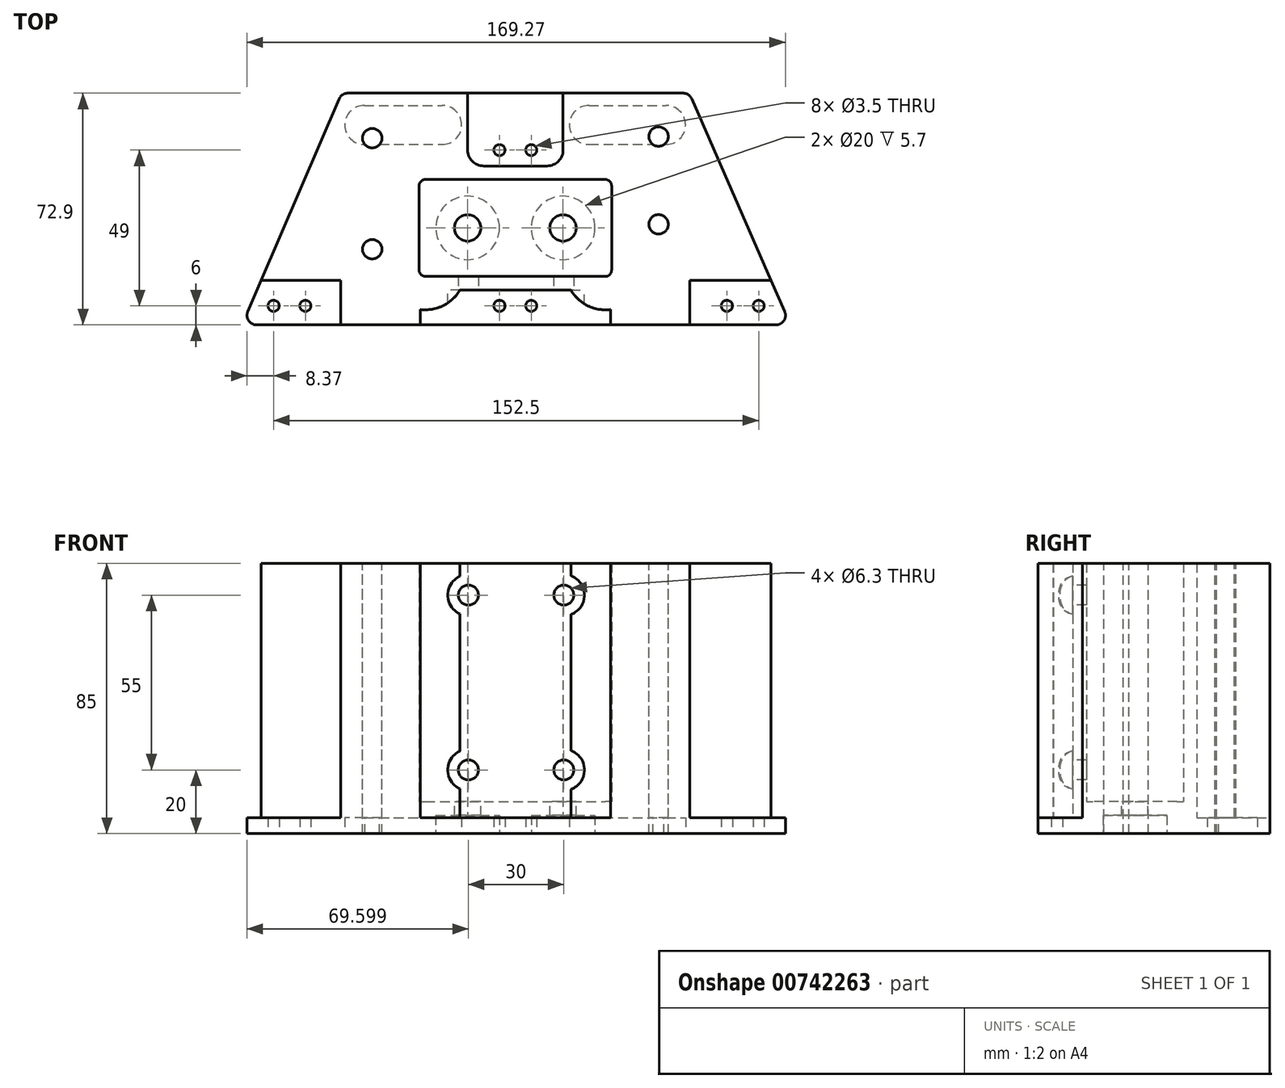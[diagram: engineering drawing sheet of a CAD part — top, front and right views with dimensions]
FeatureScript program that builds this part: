
annotation { "Feature Type Name" : "Feature", "Feature Type Description" : "" }
export const myFeature = defineFeature(function(context is Context, id is Id, definition is map)
    precondition{}
    {
        {
            var Q0;
            Q0=qCreatedBy(makeId("Top.planeOp"),FACE);
            var sketch = newSketch(context, id + "F0", { "sketchPlane" : qUnion([Q0])});
            skCircle(sketch, "E0", {"center": v(-5, 0) * mm, "radius": 1.75 * mm});
            skCircle(sketch, "E1", {"center": v(5, 0) * mm, "radius": 1.75 * mm});
            skLineSegment(sketch, "E2", {"start": v(-5, 0) * mm, "end": v(5, 0) * mm, "construction": true});
            skLineSegment(sketch, "E3.bottom", {"start": v(-47.48, 14.05) * mm, "end": v(-23.02, 14.05) * mm});
            skLineSegment(sketch, "E3.top", {"start": v(-47.48, 1.75) * mm, "end": v(-23.02, 1.75) * mm});
            skLineSegment(sketch, "E3.left", {"start": v(-47.48, 14.05) * mm, "end": v(-47.48, 1.75) * mm, "construction": true});
            skLineSegment(sketch, "E3.right", {"start": v(-23.02, 14.05) * mm, "end": v(-23.02, 1.75) * mm, "construction": true});
            skLineSegment(sketch, "E4", {"start": v(-5, 1.75) * mm, "end": v(-23.02, 1.75) * mm, "construction": true});
            skArc(sketch, "E5", {"start": v(-47.48, 14.05) * mm, "mid": v(-53.63, 7.9) * mm, "end": v(-47.48, 1.75) * mm});
            skArc(sketch, "E6", {"start": v(-23.02, 14.05) * mm, "mid": v(-16.88, 7.9) * mm, "end": v(-23.02, 1.75) * mm});
            skLineSegment(sketch, "E7", {"start": v(-53.63, 7.9) * mm, "end": v(-16.88, 7.9) * mm, "construction": true});
            skLineSegment(sketch, "E8", {"start": v(-16.88, 7.9) * mm, "end": v(-16.88, 1.75) * mm, "construction": true});
            skLineSegment(sketch, "E9", {"start": v(-5, 0) * mm, "end": v(-5, 1.75) * mm, "construction": true});
            skLineSegment(sketch, "E10.bottom", {"start": v(23.15, 14.05) * mm, "end": v(47.35, 14.05) * mm});
            skLineSegment(sketch, "E10.top", {"start": v(23.15, 1.75) * mm, "end": v(47.35, 1.75) * mm});
            skLineSegment(sketch, "E10.left", {"start": v(23.15, 14.05) * mm, "end": v(23.15, 1.75) * mm, "construction": true});
            skLineSegment(sketch, "E10.right", {"start": v(47.35, 14.05) * mm, "end": v(47.35, 1.75) * mm, "construction": true});
            skArc(sketch, "E11", {"start": v(23.15, 14.05) * mm, "mid": v(17, 7.9) * mm, "end": v(23.15, 1.75) * mm});
            skArc(sketch, "E12", {"start": v(47.35, 14.05) * mm, "mid": v(53.5, 7.9) * mm, "end": v(47.35, 1.75) * mm});
            skLineSegment(sketch, "E13", {"start": v(17, 7.9) * mm, "end": v(53.5, 7.9) * mm, "construction": true});
            skLineSegment(sketch, "E14", {"start": v(23.15, 1.75) * mm, "end": v(5, 1.75) * mm, "construction": true});
            skLineSegment(sketch, "E15", {"start": v(5, 0) * mm, "end": v(5, 1.75) * mm, "construction": true});
            skLineSegment(sketch, "E16", {"start": v(17, 7.9) * mm, "end": v(17, 1.75) * mm, "construction": true});
            skLineSegment(sketch, "E17", {"start": v(-5, 0) * mm, "end": v(-5, -49) * mm, "construction": true});
            skCircle(sketch, "E18", {"center": v(-5, -49) * mm, "radius": 1.75 * mm});
            skLineSegment(sketch, "E19", {"start": v(-5, -49) * mm, "end": v(5, -49) * mm, "construction": true});
            skCircle(sketch, "E20", {"center": v(5, -49) * mm, "radius": 1.75 * mm});
            skLineSegment(sketch, "E21", {"start": v(-5, -49) * mm, "end": v(-66, -49) * mm, "construction": true});
            skLineSegment(sketch, "E22", {"start": v(-76, -49) * mm, "end": v(-66, -49) * mm, "construction": true});
            skLineSegment(sketch, "E23", {"start": v(5, -49) * mm, "end": v(66.5, -49) * mm, "construction": true});
            skLineSegment(sketch, "E24", {"start": v(66.5, -49) * mm, "end": v(76.5, -49) * mm, "construction": true});
            skCircle(sketch, "E25", {"center": v(76.5, -49) * mm, "radius": 1.75 * mm});
            skCircle(sketch, "E26", {"center": v(66.5, -49) * mm, "radius": 1.75 * mm});
            skCircle(sketch, "E27", {"center": v(-76, -49) * mm, "radius": 1.75 * mm});
            skCircle(sketch, "E28", {"center": v(-66, -49) * mm, "radius": 1.75 * mm});
            skLineSegment(sketch, "E29", {"start": v(-55.42, 16.08) * mm, "end": v(-84.12, -50.82) * mm});
            skLineSegment(sketch, "E30", {"start": v(-81.37, -55) * mm, "end": v(81.9, -55) * mm});
            skLineSegment(sketch, "E31", {"start": v(84.65, -50.8) * mm, "end": v(55.43, 16.1) * mm});
            skLineSegment(sketch, "E32", {"start": v(52.68, 17.9) * mm, "end": v(-52.67, 17.9) * mm});
            skLineSegment(sketch, "E33", {"start": v(0, 0) * mm, "end": v(0, 17.9) * mm, "construction": true});
            skPoint(sketch, "E34.visualSharp", {"position": v(-85.92, -55) * mm});
            skArc(sketch, "E34.filletArc", {"start": v(-84.12, -50.82) * mm, "mid": v(-83.87, -53.65) * mm, "end": v(-81.37, -55) * mm});
            skPoint(sketch, "E35.visualSharp", {"position": v(-54.64, 17.9) * mm});
            skArc(sketch, "E35.filletArc", {"start": v(-52.67, 17.9) * mm, "mid": v(-54.32, 17.4) * mm, "end": v(-55.42, 16.08) * mm});
            skPoint(sketch, "E36.visualSharp", {"position": v(54.64, 17.9) * mm});
            skArc(sketch, "E36.filletArc", {"start": v(55.43, 16.1) * mm, "mid": v(54.32, 17.41) * mm, "end": v(52.68, 17.9) * mm});
            skPoint(sketch, "E37.visualSharp", {"position": v(86.49, -55) * mm});
            skArc(sketch, "E37.filletArc", {"start": v(81.9, -55) * mm, "mid": v(84.41, -53.64) * mm, "end": v(84.65, -50.8) * mm});
            skLineSegment(sketch, "E38", {"start": v(-77.6, -48.31) * mm, "end": v(-82.2, -46.34) * mm, "construction": true});
            skLineSegment(sketch, "E39", {"start": v(-77.6, -48.31) * mm, "end": v(-76, -49) * mm, "construction": true});
            skLineSegment(sketch, "E40", {"start": v(76.5, -49) * mm, "end": v(78.1, -48.3) * mm, "construction": true});
            skLineSegment(sketch, "E41", {"start": v(78.1, -48.3) * mm, "end": v(82.69, -46.3) * mm, "construction": true});
            skLineSegment(sketch, "E42", {"start": v(0, 0) * mm, "end": v(0, -49) * mm, "construction": true});
            skPoint(sketch, "E43", {"position": v(-35.25, 7.9) * mm});
            skPoint(sketch, "E44", {"position": v(35.25, 7.9) * mm});
            skSolve(sketch);
        }
        {
            var Q0;
            Q0 = qSketchRegion(id + "F0", true);
            var Q1;
            Q1=makeQuery(id+"F0.imprint","IMPRINT",FACE,{"disambiguationData":[TD([[makeQuery(id+"F0.imprint","IMPRINT",EDGE,{"derivedFrom":sQuery(id+"F0.wireOp",EDGE,"E3.bottom")}),-1.0]])]});
            var Q2;
            Q2=makeQuery(id+"F0.imprint","IMPRINT",FACE,{"disambiguationData":[TD([[makeQuery(id+"F0.imprint","IMPRINT",EDGE,{"derivedFrom":sQuery(id+"F0.wireOp",EDGE,"E10.bottom")}),-1.0]])]});
            extrude(context, id + "F1", {"entities" : qUnion([Q0, Q1, Q2]), "depth" : 5 * mm, "offsetDistance" : 25 * mm});
        }
        {
            var Q0;
            Q0=makeQuery(id+"F1.opExtrude","CAP_FACE",FACE,{"disambiguationData":[OSD([sQuery(id+"F0.wireOp",EDGE,"E0"),sQuery(id+"F0.wireOp",EDGE,"E1"),sQuery(id+"F0.wireOp",EDGE,"E18"),sQuery(id+"F0.wireOp",EDGE,"E20"),sQuery(id+"F0.wireOp",EDGE,"E25"),sQuery(id+"F0.wireOp",EDGE,"E26"),sQuery(id+"F0.wireOp",EDGE,"E27"),sQuery(id+"F0.wireOp",EDGE,"E28"),sQuery(id+"F0.wireOp",EDGE,"E29"),sQuery(id+"F0.wireOp",EDGE,"E30"),sQuery(id+"F0.wireOp",EDGE,"E31"),sQuery(id+"F0.wireOp",EDGE,"E32"),sQuery(id+"F0.wireOp",EDGE,"E34.filletArc"),sQuery(id+"F0.wireOp",EDGE,"E35.filletArc"),sQuery(id+"F0.wireOp",EDGE,"E36.filletArc"),sQuery(id+"F0.wireOp",EDGE,"E37.filletArc")])],"isStart":false});
            var sketch = newSketch(context, id + "F2", { "sketchPlane" : qUnion([Q0])});
            skLineSegment(sketch, "E45.bottom", {"start": v(-28.25, -9.25) * mm, "end": v(28.25, -9.25) * mm});
            skLineSegment(sketch, "E45.top", {"start": v(-28.25, -39.75) * mm, "end": v(28.25, -39.75) * mm});
            skLineSegment(sketch, "E45.left", {"start": v(-30.25, -11.25) * mm, "end": v(-30.25, -37.75) * mm});
            skLineSegment(sketch, "E45.right", {"start": v(30.25, -11.25) * mm, "end": v(30.25, -37.75) * mm});
            skPoint(sketch, "E46.visualSharp", {"position": v(-30.25, -9.25) * mm});
            skArc(sketch, "E46.filletArc", {"start": v(-28.25, -9.25) * mm, "mid": v(-29.66, -9.84) * mm, "end": v(-30.25, -11.25) * mm});
            skPoint(sketch, "E47.visualSharp", {"position": v(30.25, -9.25) * mm});
            skArc(sketch, "E47.filletArc", {"start": v(30.25, -11.25) * mm, "mid": v(29.66, -9.84) * mm, "end": v(28.25, -9.25) * mm});
            skPoint(sketch, "E48.visualSharp", {"position": v(30.25, -39.75) * mm});
            skArc(sketch, "E48.filletArc", {"start": v(28.25, -39.75) * mm, "mid": v(29.66, -39.16) * mm, "end": v(30.25, -37.75) * mm});
            skPoint(sketch, "E49.visualSharp", {"position": v(-30.25, -39.75) * mm});
            skArc(sketch, "E49.filletArc", {"start": v(-30.25, -37.75) * mm, "mid": v(-29.66, -39.16) * mm, "end": v(-28.25, -39.75) * mm});
            skLineSegment(sketch, "E50.0", {"start": v(-28.05, -11.45) * mm, "end": v(28.05, -11.45) * mm, "construction": true});
            skLineSegment(sketch, "E50.1", {"start": v(-28.05, -11.45) * mm, "end": v(-28.05, -37.55) * mm, "construction": true});
            skLineSegment(sketch, "E50.2", {"start": v(-28.05, -37.55) * mm, "end": v(28.05, -37.55) * mm, "construction": true});
            skLineSegment(sketch, "E50.3", {"start": v(28.05, -11.45) * mm, "end": v(28.05, -37.55) * mm, "construction": true});
            skLineSegment(sketch, "E51", {"start": v(-30.25, -24.5) * mm, "end": v(30.25, -24.5) * mm, "construction": true});
            skCircle(sketch, "E52", {"center": v(-15, -24.5) * mm, "radius": 4.15 * mm});
            skCircle(sketch, "E53", {"center": v(15, -24.5) * mm, "radius": 4.15 * mm});
            skLineSegment(sketch, "E54.0", {"start": v(-55.42, 16.08) * mm, "end": v(-84.12, -50.82) * mm});
            skArc(sketch, "E54.1", {"start": v(-52.67, 17.9) * mm, "mid": v(-54.32, 17.4) * mm, "end": v(-55.42, 16.08) * mm});
            skLineSegment(sketch, "E54.2", {"start": v(52.68, 17.9) * mm, "end": v(-52.67, 17.9) * mm});
            skArc(sketch, "E54.3", {"start": v(55.43, 16.1) * mm, "mid": v(54.32, 17.41) * mm, "end": v(52.68, 17.9) * mm});
            skLineSegment(sketch, "E54.4", {"start": v(84.65, -50.8) * mm, "end": v(55.43, 16.1) * mm});
            skArc(sketch, "E54.5", {"start": v(81.9, -55) * mm, "mid": v(84.41, -53.64) * mm, "end": v(84.65, -50.8) * mm});
            skLineSegment(sketch, "E54.6", {"start": v(-81.37, -55) * mm, "end": v(81.9, -55) * mm});
            skArc(sketch, "E54.7", {"start": v(-84.12, -50.82) * mm, "mid": v(-83.87, -53.65) * mm, "end": v(-81.37, -55) * mm});
            skArc(sketch, "E55", {"start": v(17.42, -44) * mm, "mid": v(29.87, -50.14) * mm, "end": v(40.32, -41) * mm});
            skArc(sketch, "E56", {"start": v(-40.32, -41) * mm, "mid": v(-29.87, -50.14) * mm, "end": v(-17.42, -44) * mm});
            skLineSegment(sketch, "E57", {"start": v(-79.91, -41) * mm, "end": v(-40.32, -41) * mm});
            skLineSegment(sketch, "E58", {"start": v(-17.42, -44) * mm, "end": v(17.42, -44) * mm});
            skLineSegment(sketch, "E59", {"start": v(-15, -5) * mm, "end": v(15, -5) * mm});
            skLineSegment(sketch, "E60", {"start": v(-15, -5) * mm, "end": v(-15, 17.9) * mm});
            skLineSegment(sketch, "E61", {"start": v(15, -5) * mm, "end": v(15, 17.9) * mm});
            skLineSegment(sketch, "E62", {"start": v(40.32, -41) * mm, "end": v(80.37, -41) * mm});
            skPoint(sketch, "E63", {"position": v(0, -5) * mm});
            skSolve(sketch);
        }
        {
            var Q0;
            Q0=makeQuery(id+"F2.imprint","IMPRINT",FACE,{"disambiguationData":[TD([[makeQuery(id+"F2.imprint","IMPRINT",EDGE,{"derivedFrom":sQuery(id+"F2.wireOp",EDGE,"E45.bottom")}),1.0]])]});
            extrude(context, id + "F3", {"entities" : qUnion([Q0]), "operationType" : NewBodyOperationType.ADD, "depth" : 80 * mm, "offsetDistance" : 25 * mm});
        }
        {
            var Q0;
            Q0=makeQuery(id+"F2.imprint","IMPRINT",FACE,{"disambiguationData":[TD([[makeQuery(id+"F2.imprint","IMPRINT",EDGE,{"derivedFrom":sQuery(id+"F2.wireOp",EDGE,"E52")}),1.0]])]});
            var Q1;
            Q1=makeQuery(id+"F2.imprint","IMPRINT",FACE,{"disambiguationData":[TD([[makeQuery(id+"F2.imprint","IMPRINT",EDGE,{"derivedFrom":sQuery(id+"F2.wireOp",EDGE,"E53")}),1.0]])]});
            extrude(context, id + "F4", {"entities" : qUnion([Q0, Q1]), "operationType" : NewBodyOperationType.REMOVE, "endBound" : BoundingType.THROUGH_ALL, "oppositeDirection" : true, "depth" : 25 * mm, "offsetDistance" : 25 * mm});
        }
        {
            var Q0;
            Q0=makeQuery(id+"F3.opExtrude","SWEPT_FACE",FACE,{"disambiguationData":[OSD([sQuery(id+"F2.wireOp",EDGE,"E58")])]});
            var sketch = newSketch(context, id + "F5", { "sketchPlane" : qUnion([Q0])});
            skLineSegment(sketch, "E64", {"start": v(-79.91, 20) * mm, "end": v(80.37, 20) * mm, "construction": true});
            skLineSegment(sketch, "E65", {"start": v(-79.91, 75) * mm, "end": v(80.37, 75) * mm, "construction": true});
            skCircle(sketch, "E66", {"center": v(-14.77, 75) * mm, "radius": 3.15 * mm});
            skCircle(sketch, "E67", {"center": v(15.23, 75) * mm, "radius": 3.15 * mm});
            skCircle(sketch, "E68", {"center": v(-14.77, 20) * mm, "radius": 3.15 * mm});
            skCircle(sketch, "E69", {"center": v(15.23, 20) * mm, "radius": 3.15 * mm});
            skLineSegment(sketch, "E70", {"start": v(-14.77, 75) * mm, "end": v(-14.77, 20) * mm, "construction": true});
            skLineSegment(sketch, "E71", {"start": v(15.23, 75) * mm, "end": v(15.23, 20) * mm, "construction": true});
            skPoint(sketch, "E72", {"position": v(0.23, 75) * mm});
            skCircle(sketch, "E73", {"center": v(-14.77, 75) * mm, "radius": 6.5 * mm});
            skCircle(sketch, "E74", {"center": v(15.23, 75) * mm, "radius": 6.5 * mm});
            skCircle(sketch, "E75", {"center": v(15.23, 20) * mm, "radius": 6.5 * mm});
            skCircle(sketch, "E76", {"center": v(-14.77, 20) * mm, "radius": 6.5 * mm});
            skSolve(sketch);
        }
        {
            var Q0;
            {var subQ0=sQuery(id+"F5.wireOp",EDGE,"E66");var subQ1=makeQuery(id+"F3.opExtrude","SWEPT_EDGE",EDGE,{"disambiguationData":[OSD([sQuery(id+"F2.wireOp",EDGE,"E56"),sQuery(id+"F2.wireOp",EDGE,"E58")])]});var subQ2=makeQuery(id+"F5.imprint","INTERSECT",VERTEX,{"disambiguationData":[OD(0.0)],"derivedFrom":[subQ1,subQ0]});Q0=makeQuery(id+"F5.imprint","IMPRINT",FACE,{"disambiguationData":[TD([[makeQuery(id+"F5.imprint","IMPRINT",EDGE,{"disambiguationData":[TD([[subQ2,1.0]])],"derivedFrom":subQ0}),1.0]])]});}
            var Q1;
            {var subQ0=sQuery(id+"F5.wireOp",EDGE,"E67");var subQ1=makeQuery(id+"F3.opExtrude","SWEPT_EDGE",EDGE,{"disambiguationData":[OSD([sQuery(id+"F2.wireOp",EDGE,"E55"),sQuery(id+"F2.wireOp",EDGE,"E58")])]});var subQ2=makeQuery(id+"F5.imprint","INTERSECT",VERTEX,{"disambiguationData":[OD(0.0)],"derivedFrom":[subQ1,subQ0]});Q1=makeQuery(id+"F5.imprint","IMPRINT",FACE,{"disambiguationData":[TD([[makeQuery(id+"F5.imprint","IMPRINT",EDGE,{"disambiguationData":[TD([[subQ2,-1.0]])],"derivedFrom":subQ0}),1.0]])]});}
            var Q2;
            {var subQ0=sQuery(id+"F5.wireOp",EDGE,"E69");var subQ1=makeQuery(id+"F3.opExtrude","SWEPT_EDGE",EDGE,{"disambiguationData":[OSD([sQuery(id+"F2.wireOp",EDGE,"E55"),sQuery(id+"F2.wireOp",EDGE,"E58")])]});var subQ2=makeQuery(id+"F5.imprint","INTERSECT",VERTEX,{"disambiguationData":[OD(0.0)],"derivedFrom":[subQ1,subQ0]});Q2=makeQuery(id+"F5.imprint","IMPRINT",FACE,{"disambiguationData":[TD([[makeQuery(id+"F5.imprint","IMPRINT",EDGE,{"disambiguationData":[TD([[subQ2,1.0]])],"derivedFrom":subQ0}),1.0]])]});}
            var Q3;
            {var subQ0=sQuery(id+"F5.wireOp",EDGE,"E68");var subQ1=makeQuery(id+"F3.opExtrude","SWEPT_EDGE",EDGE,{"disambiguationData":[OSD([sQuery(id+"F2.wireOp",EDGE,"E56"),sQuery(id+"F2.wireOp",EDGE,"E58")])]});var subQ2=makeQuery(id+"F5.imprint","INTERSECT",VERTEX,{"disambiguationData":[OD(0.0)],"derivedFrom":[subQ1,subQ0]});Q3=makeQuery(id+"F5.imprint","IMPRINT",FACE,{"disambiguationData":[TD([[makeQuery(id+"F5.imprint","IMPRINT",EDGE,{"disambiguationData":[TD([[subQ2,-1.0]])],"derivedFrom":subQ0}),1.0]])]});}
            var Q4;
            {var subQ0=sQuery(id+"F5.wireOp",EDGE,"E68");var subQ1=makeQuery(id+"F3.opExtrude","SWEPT_EDGE",EDGE,{"disambiguationData":[OSD([sQuery(id+"F2.wireOp",EDGE,"E56"),sQuery(id+"F2.wireOp",EDGE,"E58")])]});var subQ2=makeQuery(id+"F5.imprint","INTERSECT",VERTEX,{"disambiguationData":[OD(0.0)],"derivedFrom":[subQ1,subQ0]});Q4=makeQuery(id+"F5.imprint","IMPRINT",FACE,{"disambiguationData":[TD([[makeQuery(id+"F5.imprint","IMPRINT",EDGE,{"disambiguationData":[TD([[subQ2,1.0]])],"derivedFrom":subQ0}),1.0]])]});}
            var Q5;
            {var subQ0=sQuery(id+"F5.wireOp",EDGE,"E66");var subQ1=makeQuery(id+"F3.opExtrude","SWEPT_EDGE",EDGE,{"disambiguationData":[OSD([sQuery(id+"F2.wireOp",EDGE,"E56"),sQuery(id+"F2.wireOp",EDGE,"E58")])]});var subQ2=makeQuery(id+"F5.imprint","INTERSECT",VERTEX,{"disambiguationData":[OD(0.0)],"derivedFrom":[subQ1,subQ0]});Q5=makeQuery(id+"F5.imprint","IMPRINT",FACE,{"disambiguationData":[TD([[makeQuery(id+"F5.imprint","IMPRINT",EDGE,{"disambiguationData":[TD([[subQ2,-1.0]])],"derivedFrom":subQ0}),1.0]])]});}
            var Q6;
            {var subQ0=sQuery(id+"F5.wireOp",EDGE,"E67");var subQ1=makeQuery(id+"F3.opExtrude","SWEPT_EDGE",EDGE,{"disambiguationData":[OSD([sQuery(id+"F2.wireOp",EDGE,"E55"),sQuery(id+"F2.wireOp",EDGE,"E58")])]});var subQ2=makeQuery(id+"F5.imprint","INTERSECT",VERTEX,{"disambiguationData":[OD(0.0)],"derivedFrom":[subQ1,subQ0]});Q6=makeQuery(id+"F5.imprint","IMPRINT",FACE,{"disambiguationData":[TD([[makeQuery(id+"F5.imprint","IMPRINT",EDGE,{"disambiguationData":[TD([[subQ2,1.0]])],"derivedFrom":subQ0}),1.0]])]});}
            var Q7;
            {var subQ0=sQuery(id+"F5.wireOp",EDGE,"E69");var subQ1=makeQuery(id+"F3.opExtrude","SWEPT_EDGE",EDGE,{"disambiguationData":[OSD([sQuery(id+"F2.wireOp",EDGE,"E55"),sQuery(id+"F2.wireOp",EDGE,"E58")])]});var subQ2=makeQuery(id+"F5.imprint","INTERSECT",VERTEX,{"disambiguationData":[OD(0.0)],"derivedFrom":[subQ1,subQ0]});Q7=makeQuery(id+"F5.imprint","IMPRINT",FACE,{"disambiguationData":[TD([[makeQuery(id+"F5.imprint","IMPRINT",EDGE,{"disambiguationData":[TD([[subQ2,-1.0]])],"derivedFrom":subQ0}),1.0]])]});}
            extrude(context, id + "F6", {"entities" : qUnion([Q0, Q1, Q2, Q3, Q4, Q5, Q6, Q7]), "operationType" : NewBodyOperationType.REMOVE, "oppositeDirection" : true, "depth" : 25 * mm, "offsetDistance" : 25 * mm});
        }
        {
            var Q0;
            {var subQ0=sQuery(id+"F5.wireOp",EDGE,"E67");var subQ1=makeQuery(id+"F3.opExtrude","SWEPT_EDGE",EDGE,{"disambiguationData":[OSD([sQuery(id+"F2.wireOp",EDGE,"E55"),sQuery(id+"F2.wireOp",EDGE,"E58")])]});var subQ2=makeQuery(id+"F5.imprint","INTERSECT",VERTEX,{"disambiguationData":[OD(0.0)],"derivedFrom":[subQ1,subQ0]});Q0=makeQuery(id+"F5.imprint","IMPRINT",FACE,{"disambiguationData":[TD([[makeQuery(id+"F5.imprint","IMPRINT",EDGE,{"disambiguationData":[TD([[subQ2,1.0]])],"derivedFrom":subQ0}),1.0]])]});}
            var Q1;
            {var subQ0=sQuery(id+"F5.wireOp",EDGE,"E67");var subQ1=makeQuery(id+"F3.opExtrude","SWEPT_EDGE",EDGE,{"disambiguationData":[OSD([sQuery(id+"F2.wireOp",EDGE,"E55"),sQuery(id+"F2.wireOp",EDGE,"E58")])]});var subQ2=makeQuery(id+"F5.imprint","INTERSECT",VERTEX,{"disambiguationData":[OD(0.0)],"derivedFrom":[subQ1,subQ0]});Q1=makeQuery(id+"F5.imprint","IMPRINT",FACE,{"disambiguationData":[TD([[makeQuery(id+"F5.imprint","IMPRINT",EDGE,{"disambiguationData":[TD([[subQ2,1.0]])],"derivedFrom":subQ0}),-1.0]])]});}
            var Q2;
            {var subQ0=sQuery(id+"F5.wireOp",EDGE,"E69");var subQ1=makeQuery(id+"F3.opExtrude","SWEPT_EDGE",EDGE,{"disambiguationData":[OSD([sQuery(id+"F2.wireOp",EDGE,"E55"),sQuery(id+"F2.wireOp",EDGE,"E58")])]});var subQ2=makeQuery(id+"F5.imprint","INTERSECT",VERTEX,{"disambiguationData":[OD(0.0)],"derivedFrom":[subQ1,subQ0]});Q2=makeQuery(id+"F5.imprint","IMPRINT",FACE,{"disambiguationData":[TD([[makeQuery(id+"F5.imprint","IMPRINT",EDGE,{"disambiguationData":[TD([[subQ2,-1.0]])],"derivedFrom":subQ0}),-1.0]])]});}
            var Q3;
            {var subQ0=sQuery(id+"F5.wireOp",EDGE,"E66");var subQ1=makeQuery(id+"F3.opExtrude","SWEPT_EDGE",EDGE,{"disambiguationData":[OSD([sQuery(id+"F2.wireOp",EDGE,"E56"),sQuery(id+"F2.wireOp",EDGE,"E58")])]});var subQ2=makeQuery(id+"F5.imprint","INTERSECT",VERTEX,{"disambiguationData":[OD(0.0)],"derivedFrom":[subQ1,subQ0]});Q3=makeQuery(id+"F5.imprint","IMPRINT",FACE,{"disambiguationData":[TD([[makeQuery(id+"F5.imprint","IMPRINT",EDGE,{"disambiguationData":[TD([[subQ2,-1.0]])],"derivedFrom":subQ0}),1.0]])]});}
            var Q4;
            {var subQ0=sQuery(id+"F5.wireOp",EDGE,"E68");var subQ1=makeQuery(id+"F3.opExtrude","SWEPT_EDGE",EDGE,{"disambiguationData":[OSD([sQuery(id+"F2.wireOp",EDGE,"E56"),sQuery(id+"F2.wireOp",EDGE,"E58")])]});var subQ2=makeQuery(id+"F5.imprint","INTERSECT",VERTEX,{"disambiguationData":[OD(0.0)],"derivedFrom":[subQ1,subQ0]});Q4=makeQuery(id+"F5.imprint","IMPRINT",FACE,{"disambiguationData":[TD([[makeQuery(id+"F5.imprint","IMPRINT",EDGE,{"disambiguationData":[TD([[subQ2,1.0]])],"derivedFrom":subQ0}),1.0]])]});}
            var Q5;
            {var subQ0=sQuery(id+"F5.wireOp",EDGE,"E69");var subQ1=makeQuery(id+"F3.opExtrude","SWEPT_EDGE",EDGE,{"disambiguationData":[OSD([sQuery(id+"F2.wireOp",EDGE,"E55"),sQuery(id+"F2.wireOp",EDGE,"E58")])]});var subQ2=makeQuery(id+"F5.imprint","INTERSECT",VERTEX,{"disambiguationData":[OD(0.0)],"derivedFrom":[subQ1,subQ0]});Q5=makeQuery(id+"F5.imprint","IMPRINT",FACE,{"disambiguationData":[TD([[makeQuery(id+"F5.imprint","IMPRINT",EDGE,{"disambiguationData":[TD([[subQ2,-1.0]])],"derivedFrom":subQ0}),1.0]])]});}
            var Q6;
            {var subQ0=sQuery(id+"F5.wireOp",EDGE,"E68");var subQ1=makeQuery(id+"F3.opExtrude","SWEPT_EDGE",EDGE,{"disambiguationData":[OSD([sQuery(id+"F2.wireOp",EDGE,"E56"),sQuery(id+"F2.wireOp",EDGE,"E58")])]});var subQ2=makeQuery(id+"F5.imprint","INTERSECT",VERTEX,{"disambiguationData":[OD(0.0)],"derivedFrom":[subQ1,subQ0]});Q6=makeQuery(id+"F5.imprint","IMPRINT",FACE,{"disambiguationData":[TD([[makeQuery(id+"F5.imprint","IMPRINT",EDGE,{"disambiguationData":[TD([[subQ2,1.0]])],"derivedFrom":subQ0}),-1.0]])]});}
            var Q7;
            {var subQ0=sQuery(id+"F5.wireOp",EDGE,"E66");var subQ1=makeQuery(id+"F3.opExtrude","SWEPT_EDGE",EDGE,{"disambiguationData":[OSD([sQuery(id+"F2.wireOp",EDGE,"E56"),sQuery(id+"F2.wireOp",EDGE,"E58")])]});var subQ2=makeQuery(id+"F5.imprint","INTERSECT",VERTEX,{"disambiguationData":[OD(0.0)],"derivedFrom":[subQ1,subQ0]});Q7=makeQuery(id+"F5.imprint","IMPRINT",FACE,{"disambiguationData":[TD([[makeQuery(id+"F5.imprint","IMPRINT",EDGE,{"disambiguationData":[TD([[subQ2,-1.0]])],"derivedFrom":subQ0}),-1.0]])]});}
            extrude(context, id + "F7", {"entities" : qUnion([Q0, Q1, Q2, Q3, Q4, Q5, Q6, Q7]), "operationType" : NewBodyOperationType.REMOVE, "endBound" : BoundingType.THROUGH_ALL, "depth" : 25 * mm, "offsetDistance" : 25 * mm});
        }
        {
            var Q0;
            Q0=makeQuery(id+"F3.opExtrude","SWEPT_EDGE",EDGE,{"disambiguationData":[OSD([sQuery(id+"F2.wireOp",EDGE,"E59"),sQuery(id+"F2.wireOp",EDGE,"E60")])]});
            var Q1;
            Q1=makeQuery(id+"F3.opExtrude","SWEPT_EDGE",EDGE,{"disambiguationData":[OSD([sQuery(id+"F2.wireOp",EDGE,"E59"),sQuery(id+"F2.wireOp",EDGE,"E61")])]});
            fillet(context, id + "F8", {"entities" : qUnion([Q0, Q1]), "radius" : 5 * mm, "tangentPropagation" : true, "allowEdgeOverflow" : false});
        }
        {
            var Q0;
            Q0=makeQuery(id+"F2.imprint","IMPRINT",FACE,{"disambiguationData":[TD([[makeQuery(id+"F2.imprint","IMPRINT",EDGE,{"derivedFrom":sQuery(id+"F2.wireOp",EDGE,"E45.bottom")}),-1.0]])]});
            extrude(context, id + "F9", {"entities" : qUnion([Q0]), "operationType" : NewBodyOperationType.ADD, "depth" : 5 * mm, "offsetDistance" : 25 * mm});
        }
        {
            var Q0;
            Q0=makeQuery(id+"F1.opExtrude","CAP_FACE",FACE,{"disambiguationData":[OSD([sQuery(id+"F0.wireOp",EDGE,"E0"),sQuery(id+"F0.wireOp",EDGE,"E1"),sQuery(id+"F0.wireOp",EDGE,"E18"),sQuery(id+"F0.wireOp",EDGE,"E20"),sQuery(id+"F0.wireOp",EDGE,"E25"),sQuery(id+"F0.wireOp",EDGE,"E26"),sQuery(id+"F0.wireOp",EDGE,"E27"),sQuery(id+"F0.wireOp",EDGE,"E28"),sQuery(id+"F0.wireOp",EDGE,"E29"),sQuery(id+"F0.wireOp",EDGE,"E30"),sQuery(id+"F0.wireOp",EDGE,"E31"),sQuery(id+"F0.wireOp",EDGE,"E32"),sQuery(id+"F0.wireOp",EDGE,"E34.filletArc"),sQuery(id+"F0.wireOp",EDGE,"E35.filletArc"),sQuery(id+"F0.wireOp",EDGE,"E36.filletArc"),sQuery(id+"F0.wireOp",EDGE,"E37.filletArc")])],"isStart":true});
            var sketch = newSketch(context, id + "F10", { "sketchPlane" : qUnion([Q0])});
            skCircle(sketch, "E77", {"center": v(-15, 24.5) * mm, "radius": 10 * mm});
            skCircle(sketch, "E78", {"center": v(15, 24.5) * mm, "radius": 10 * mm});
            skSolve(sketch);
        }
        {
            var Q0;
            Q0=makeQuery(id+"F10.imprint","IMPRINT",FACE,{"disambiguationData":[TD([[makeQuery(id+"F10.imprint","IMPRINT",EDGE,{"derivedFrom":sQuery(id+"F10.wireOp",EDGE,"E77")}),1.0]])]});
            var Q1;
            Q1=makeQuery(id+"F10.imprint","IMPRINT",FACE,{"disambiguationData":[TD([[makeQuery(id+"F10.imprint","IMPRINT",EDGE,{"derivedFrom":sQuery(id+"F10.wireOp",EDGE,"E78")}),1.0]])]});
            extrude(context, id + "F11", {"entities" : qUnion([Q0, Q1]), "operationType" : NewBodyOperationType.REMOVE, "oppositeDirection" : true, "depth" : 5.7 * mm, "offsetDistance" : 25 * mm});
        }
        {
            var Q0;
            Q0=makeQuery(id+"F0.imprint","IMPRINT",FACE,{"disambiguationData":[TD([[makeQuery(id+"F0.imprint","IMPRINT",EDGE,{"derivedFrom":sQuery(id+"F0.wireOp",EDGE,"E3.bottom")}),-1.0]])]});
            var Q1;
            Q1=makeQuery(id+"F0.imprint","IMPRINT",FACE,{"disambiguationData":[TD([[makeQuery(id+"F0.imprint","IMPRINT",EDGE,{"derivedFrom":sQuery(id+"F0.wireOp",EDGE,"E10.bottom")}),-1.0]])]});
            extrude(context, id + "F12", {"entities" : qUnion([Q0, Q1]), "operationType" : NewBodyOperationType.REMOVE, "depth" : 5 * mm, "offsetDistance" : 25 * mm});
        }
        {
            var Q0;
            Q0=makeQuery(id+"F3.opExtrude","CAP_FACE",FACE,{"disambiguationData":[OSD([sQuery(id+"F2.wireOp",EDGE,"E45.bottom"),sQuery(id+"F2.wireOp",EDGE,"E45.top"),sQuery(id+"F2.wireOp",EDGE,"E45.left"),sQuery(id+"F2.wireOp",EDGE,"E45.right"),sQuery(id+"F2.wireOp",EDGE,"E46.filletArc"),sQuery(id+"F2.wireOp",EDGE,"E47.filletArc"),sQuery(id+"F2.wireOp",EDGE,"E48.filletArc"),sQuery(id+"F2.wireOp",EDGE,"E49.filletArc"),sQuery(id+"F2.wireOp",EDGE,"E54.0"),sQuery(id+"F2.wireOp",EDGE,"E54.1"),sQuery(id+"F2.wireOp",EDGE,"E54.2"),sQuery(id+"F2.wireOp",EDGE,"E54.3"),sQuery(id+"F2.wireOp",EDGE,"E54.4"),sQuery(id+"F2.wireOp",EDGE,"E55"),sQuery(id+"F2.wireOp",EDGE,"E56"),sQuery(id+"F2.wireOp",EDGE,"E57"),sQuery(id+"F2.wireOp",EDGE,"E58"),sQuery(id+"F2.wireOp",EDGE,"E59"),sQuery(id+"F2.wireOp",EDGE,"E60"),sQuery(id+"F2.wireOp",EDGE,"E61"),sQuery(id+"F2.wireOp",EDGE,"E62")])],"isStart":false});
            var sketch = newSketch(context, id + "F13", { "sketchPlane" : qUnion([Q0])});
            skLineSegment(sketch, "E79", {"start": v(-45, 17.9) * mm, "end": v(-45, -41) * mm, "construction": true});
            skLineSegment(sketch, "E80", {"start": v(45, 17.9) * mm, "end": v(45, -41) * mm, "construction": true});
            skCircle(sketch, "E81", {"center": v(-45, 3.74) * mm, "radius": 3.05 * mm});
            skCircle(sketch, "E82", {"center": v(-45, -31.2) * mm, "radius": 3.05 * mm});
            skCircle(sketch, "E83", {"center": v(45, 4.25) * mm, "radius": 3.05 * mm});
            skCircle(sketch, "E84", {"center": v(45, -23.36) * mm, "radius": 3.05 * mm});
            skSolve(sketch);
        }
        {
            var Q0;
            {var subQ4=sQuery(id+"F2.wireOp",EDGE,"E54.5");Q0=makeQuery(id+"F2.imprint","IMPRINT",FACE,{"disambiguationData":[TD([[makeQuery(id+"F2.imprint","IMPRINT",EDGE,{"derivedFrom":subQ4}),1.0]])]});}
            var sketch = newSketch(context, id + "F14", { "sketchPlane" : qUnion([Q0])});
            skLineSegment(sketch, "E85", {"start": v(-54.87, -41) * mm, "end": v(-54.87, -55) * mm});
            skLineSegment(sketch, "E86", {"start": v(-54.87, -55) * mm, "end": v(-29.87, -55) * mm});
            skLineSegment(sketch, "E87", {"start": v(-29.87, -55) * mm, "end": v(-29.87, -50.14) * mm});
            skLineSegment(sketch, "E88", {"start": v(-54.87, -41) * mm, "end": v(-40.32, -41) * mm});
            skArc(sketch, "E89", {"start": v(-40.32, -41) * mm, "mid": v(-36.48, -47.16) * mm, "end": v(-29.87, -50.14) * mm});
            skLineSegment(sketch, "E90", {"start": v(0, -58.03) * mm, "end": v(0, 0) * mm, "construction": true});
            skLineSegment(sketch, "E91.MirrorCS", {"start": v(54.87, -41) * mm, "end": v(54.87, -55) * mm});
            skLineSegment(sketch, "E92.MirrorCS", {"start": v(54.87, -55) * mm, "end": v(29.87, -55) * mm});
            skLineSegment(sketch, "E93.MirrorCS", {"start": v(54.87, -41) * mm, "end": v(40.32, -41) * mm});
            skLineSegment(sketch, "E94.MirrorCS", {"start": v(29.87, -55) * mm, "end": v(29.87, -50.14) * mm});
            skArc(sketch, "E95.MirrorCS", {"start": v(40.32, -41) * mm, "mid": v(36.48, -47.16) * mm, "end": v(29.87, -50.14) * mm});
            skSolve(sketch);
        }
        {
            var Q0;
            Q0=makeQuery(id+"F14.imprint","IMPRINT",FACE,{"disambiguationData":[TD([[makeQuery(id+"F14.imprint","IMPRINT",EDGE,{"derivedFrom":sQuery(id+"F14.wireOp",EDGE,"E85")}),1.0]])]});
            var Q1;
            Q1=makeQuery(id+"F14.imprint","IMPRINT",FACE,{"disambiguationData":[TD([[makeQuery(id+"F14.imprint","IMPRINT",EDGE,{"derivedFrom":sQuery(id+"F14.wireOp",EDGE,"E91.MirrorCS")}),-1.0]])]});
            var Q2;
            Q2=makeQuery(id+"F3.opExtrude","CAP_FACE",FACE,{"disambiguationData":[OSD([sQuery(id+"F2.wireOp",EDGE,"E45.bottom"),sQuery(id+"F2.wireOp",EDGE,"E45.top"),sQuery(id+"F2.wireOp",EDGE,"E45.left"),sQuery(id+"F2.wireOp",EDGE,"E45.right"),sQuery(id+"F2.wireOp",EDGE,"E46.filletArc"),sQuery(id+"F2.wireOp",EDGE,"E47.filletArc"),sQuery(id+"F2.wireOp",EDGE,"E48.filletArc"),sQuery(id+"F2.wireOp",EDGE,"E49.filletArc"),sQuery(id+"F2.wireOp",EDGE,"E54.0"),sQuery(id+"F2.wireOp",EDGE,"E54.1"),sQuery(id+"F2.wireOp",EDGE,"E54.2"),sQuery(id+"F2.wireOp",EDGE,"E54.3"),sQuery(id+"F2.wireOp",EDGE,"E54.4"),sQuery(id+"F2.wireOp",EDGE,"E55"),sQuery(id+"F2.wireOp",EDGE,"E56"),sQuery(id+"F2.wireOp",EDGE,"E57"),sQuery(id+"F2.wireOp",EDGE,"E58"),sQuery(id+"F2.wireOp",EDGE,"E59"),sQuery(id+"F2.wireOp",EDGE,"E60"),sQuery(id+"F2.wireOp",EDGE,"E61"),sQuery(id+"F2.wireOp",EDGE,"E62")])],"isStart":false});
            extrude(context, id + "F15", {"entities" : qUnion([Q0, Q1]), "operationType" : NewBodyOperationType.ADD, "endBound" : BoundingType.UP_TO_SURFACE, "depth" : 25 * mm, "endBoundEntityFace" : qUnion([Q2]), "offsetDistance" : 25 * mm});
        }
        {
            var Q0;
            Q0 = qSketchRegion(id + "F13", true);
            extrude(context, id + "F16", {"entities" : qUnion([Q0]), "operationType" : NewBodyOperationType.REMOVE, "endBound" : BoundingType.THROUGH_ALL, "oppositeDirection" : true, "depth" : 25 * mm, "offsetDistance" : 25 * mm});
        }
    });
